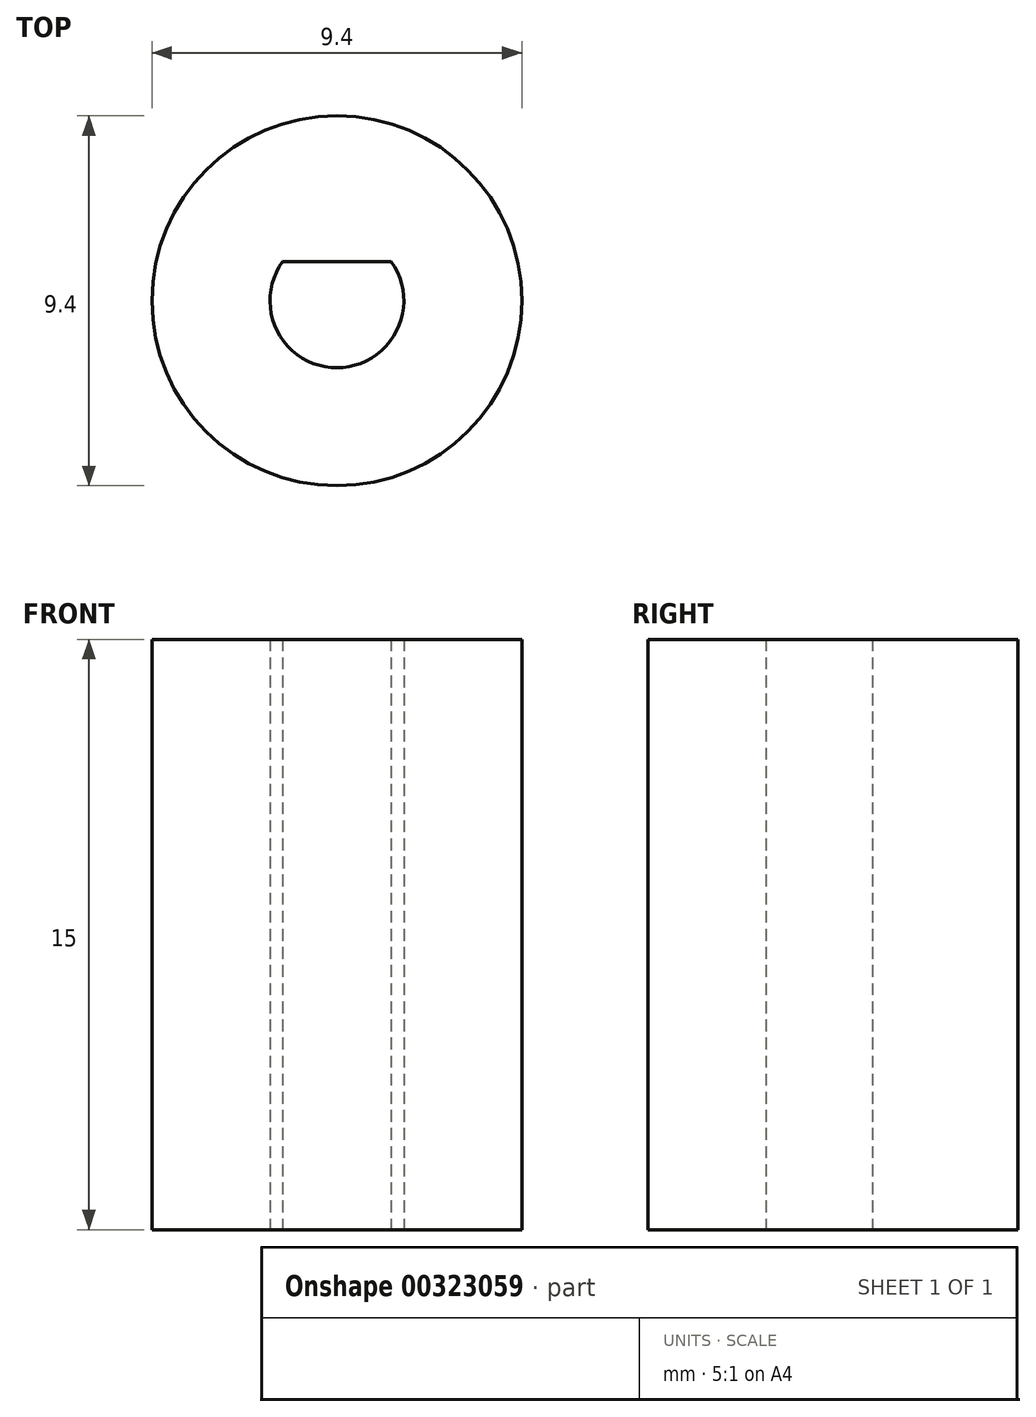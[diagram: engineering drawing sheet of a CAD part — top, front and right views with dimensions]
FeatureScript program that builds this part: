
annotation { "Feature Type Name" : "Feature", "Feature Type Description" : "" }
export const myFeature = defineFeature(function(context is Context, id is Id, definition is map)
    precondition{}
    {
        {
            var Q0;
            Q0=qCreatedBy(makeId("Top.planeOp"),FACE);
            var sketch = newSketch(context, id + "F0", { "sketchPlane" : qUnion([Q0])});
            skCircle(sketch, "E0", {"center": v(0, 0) * mm, "radius": 1.7 * mm});
            skCircle(sketch, "E1", {"center": v(0, 0) * mm, "radius": 4.7 * mm});
            skLineSegment(sketch, "E2", {"start": v(-1.37, 1) * mm, "end": v(1.37, 1) * mm});
            skSolve(sketch);
        }
        {
            var Q0;
            Q0=makeQuery(id+"F0.imprint","IMPRINT",FACE,{"disambiguationData":[TD([[makeQuery(id+"F0.imprint","IMPRINT",EDGE,{"derivedFrom":sQuery(id+"F0.wireOp",EDGE,"E1")}),1.0]])]});
            var Q1;
            {var subQ0=sQuery(id+"F0.wireOp",EDGE,"E2");Q1=makeQuery(id+"F0.imprint","IMPRINT",FACE,{"disambiguationData":[TD([[makeQuery(id+"F0.imprint","IMPRINT",EDGE,{"derivedFrom":subQ0}),1.0]])]});}
            extrude(context, id + "F1", {"entities" : qUnion([Q0, Q1]), "endBound" : BoundingType.SYMMETRIC, "depth" : 15 * mm});
        }
    });
